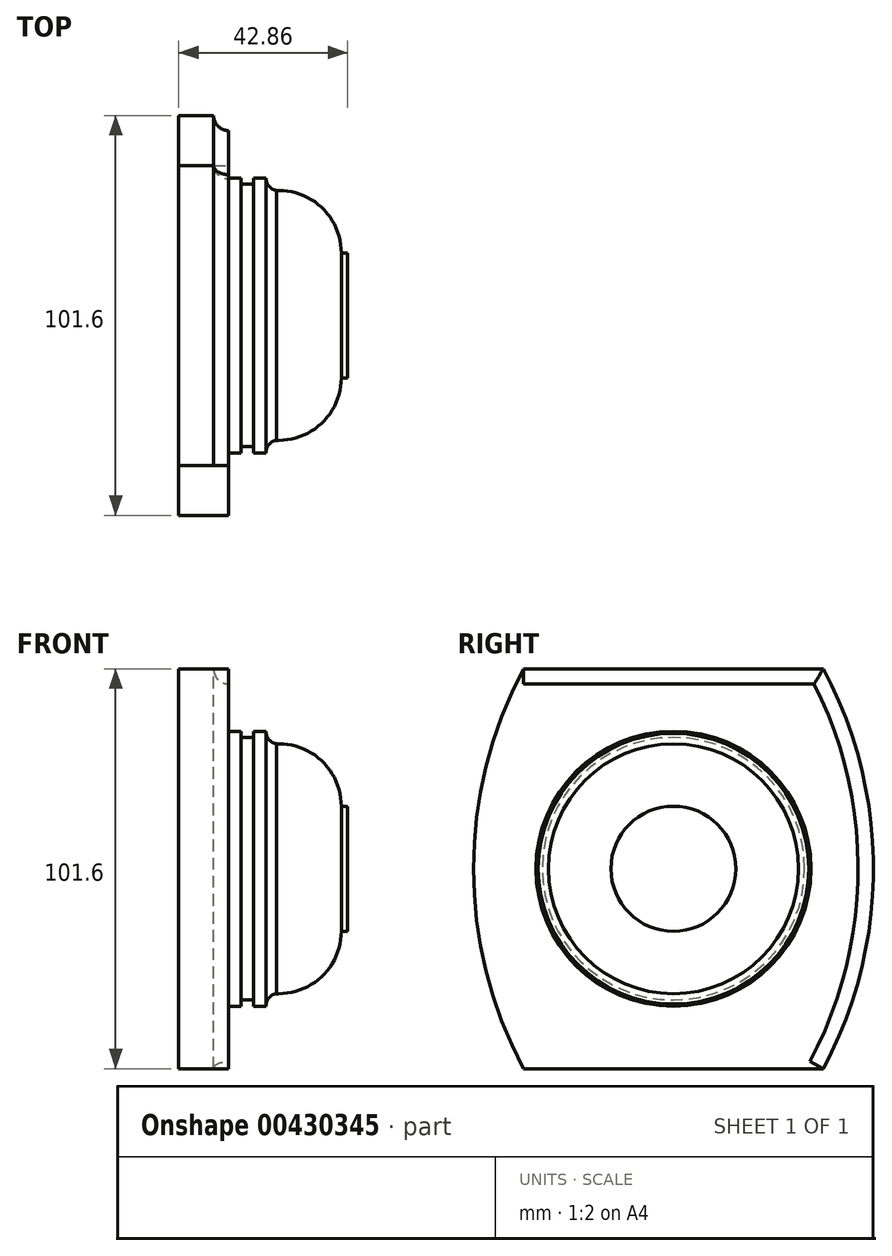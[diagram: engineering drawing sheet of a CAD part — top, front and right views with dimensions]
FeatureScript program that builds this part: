
annotation { "Feature Type Name" : "Feature", "Feature Type Description" : "" }
export const myFeature = defineFeature(function(context is Context, id is Id, definition is map)
    precondition{}
    {
        {
            var Q0;
            Q0=qCreatedBy(makeId("Front.planeOp"),FACE);
            var sketch = newSketch(context, id + "F0", { "sketchPlane" : qUnion([Q0])});
            skLineSegment(sketch, "E0", {"start": v(0, 0) * mm, "end": v(0, 34.93) * mm});
            skLineSegment(sketch, "E1", {"start": v(0, 34.93) * mm, "end": v(3.18, 34.93) * mm});
            skLineSegment(sketch, "E2", {"start": v(3.18, 34.93) * mm, "end": v(3.18, 33.34) * mm});
            skLineSegment(sketch, "E3", {"start": v(3.18, 33.34) * mm, "end": v(6.35, 33.34) * mm});
            skLineSegment(sketch, "E4", {"start": v(6.35, 33.34) * mm, "end": v(6.35, 34.93) * mm});
            skLineSegment(sketch, "E5", {"start": v(6.35, 34.93) * mm, "end": v(9.53, 34.93) * mm});
            skLineSegment(sketch, "E6", {"start": v(9.53, 34.93) * mm, "end": v(9.53, 34.36) * mm});
            skLineSegment(sketch, "E7", {"start": v(12.14, 31.75) * mm, "end": v(12.7, 31.75) * mm});
            skLineSegment(sketch, "E8", {"start": v(12.7, 31.75) * mm, "end": v(12.7, 31.75) * mm});
            skLineSegment(sketch, "E9", {"start": v(28.58, 15.88) * mm, "end": v(28.58, 15.88) * mm});
            skPoint(sketch, "E10.visualSharp", {"position": v(28.58, 31.75) * mm});
            skArc(sketch, "E10.filletArc", {"start": v(28.58, 15.88) * mm, "mid": v(23.93, 27.1) * mm, "end": v(12.7, 31.75) * mm});
            skArc(sketch, "E11", {"start": v(9.53, 34.93) * mm, "mid": v(10.36, 32.59) * mm, "end": v(12.7, 31.75) * mm});
            skPoint(sketch, "E11.third.point", {"position": v(15.1, 35.76) * mm});
            skLineSegment(sketch, "E12", {"start": v(28.58, 15.88) * mm, "end": v(30.16, 15.88) * mm});
            skLineSegment(sketch, "E13", {"start": v(30.16, 15.88) * mm, "end": v(30.16, 0) * mm});
            skLineSegment(sketch, "E14", {"start": v(30.16, 0) * mm, "end": v(0, 0) * mm});
            skSolve(sketch);
        }
        {
            var Q0;
            Q0 = qSketchRegion(id + "F0", true);
            var Q1;
            Q1=sQuery(id+"F0.wireOp",EDGE,"E14");
            revolve(context, id + "F1", {"entities" : qUnion([Q0]), "axis" : qUnion([Q1]), "revolveType" : RevolveType.FULL});
        }
        {
            var Q0;
            Q0=qCreatedBy(makeId("Right.planeOp"),FACE);
            var sketch = newSketch(context, id + "F2", { "sketchPlane" : qUnion([Q0])});
            skLineSegment(sketch, "E15.bottom", {"start": v(-38.1, 50.8) * mm, "end": v(38.1, 50.8) * mm});
            skLineSegment(sketch, "E15.top", {"start": v(-38.1, -50.8) * mm, "end": v(38.1, -50.8) * mm});
            skLineSegment(sketch, "E16", {"start": v(0, 0) * mm, "end": v(0, 50.8) * mm, "construction": true});
            skLineSegment(sketch, "E17", {"start": v(0, 0) * mm, "end": v(-50.8, 0) * mm, "construction": true});
            skLineSegment(sketch, "E18", {"start": v(0, 0) * mm, "end": v(50.8, 0) * mm});
            skLineSegment(sketch, "E19", {"start": v(-38.1, 50.8) * mm, "end": v(-38.1, -50.8) * mm, "construction": true});
            skArc(sketch, "E20", {"start": v(-38.1, 50.8) * mm, "mid": v(-50.8, 0) * mm, "end": v(-38.1, -50.8) * mm});
            skPoint(sketch, "E21.orphan", {"position": v(-50.8, 50.8) * mm});
            skPoint(sketch, "E22.orphan", {"position": v(-50.8, -50.8) * mm});
            skArc(sketch, "E23.MirrorCS", {"start": v(38.1, 50.8) * mm, "mid": v(50.8, 0) * mm, "end": v(38.1, -50.8) * mm});
            skPoint(sketch, "E24.orphan", {"position": v(50.8, 50.8) * mm});
            skPoint(sketch, "E15.right.end.orphan", {"position": v(50.8, -50.8) * mm});
            skSolve(sketch);
        }
        {
            var Q0;
            Q0 = qSketchRegion(id + "F2", true);
            extrude(context, id + "F3", {"entities" : qUnion([Q0]), "operationType" : NewBodyOperationType.ADD, "oppositeDirection" : true, "depth" : 12.7 * mm});
        }
        {
            var Q0;
            Q0=qCreatedBy(makeId("Front.planeOp"),FACE);
            var sketch = newSketch(context, id + "F4", { "sketchPlane" : qUnion([Q0])});
            skCircle(sketch, "E25", {"center": v(0, 50.8) * mm, "radius": 3.87 * mm});
            skSolve(sketch);
        }
        {
            var Q0;
            Q0 = qSketchRegion(id + "F4", true);
            var Q1;
            Q1=makeQuery(id+"F3.opExtrude","CAP_EDGE",EDGE,{"disambiguationData":[OSD([sQuery(id+"F2.wireOp",EDGE,"E15.bottom")])],"isStart":true});
            var Q2;
            Q2=makeQuery(id+"F3.opExtrude","CAP_EDGE",EDGE,{"disambiguationData":[OSD([sQuery(id+"F2.wireOp",EDGE,"E23.MirrorCS")])],"isStart":true});
            sweep(context, id + "F5", {"operationType" : NewBodyOperationType.REMOVE, "profiles" : qUnion([Q0]), "path" : qUnion([Q1, Q2])});
        }
    });
